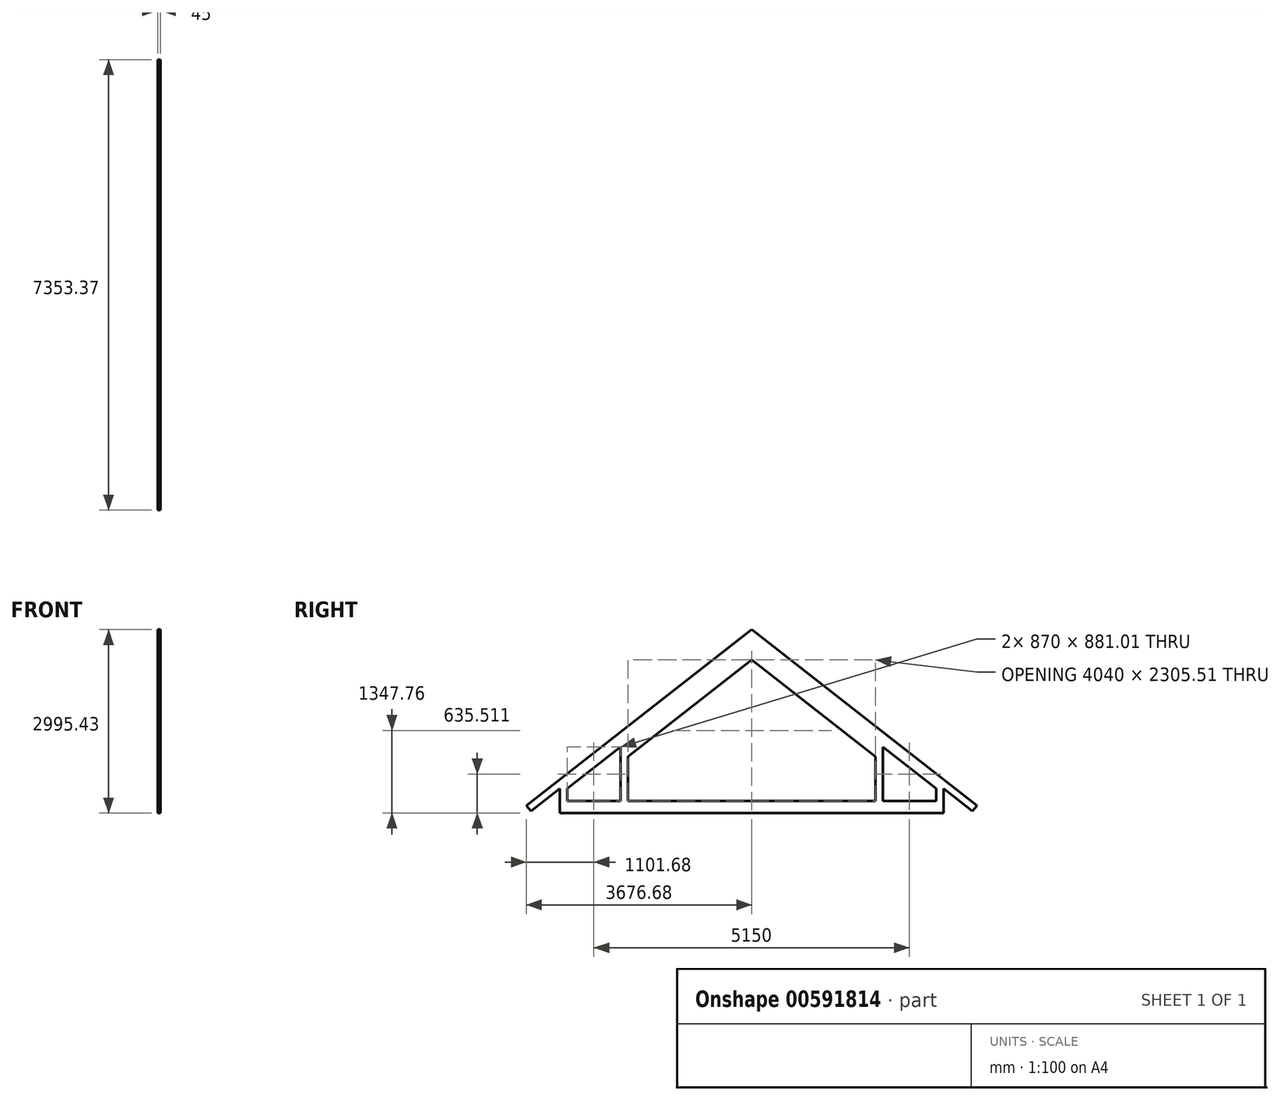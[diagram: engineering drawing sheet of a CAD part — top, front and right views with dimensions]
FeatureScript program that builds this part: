
annotation { "Feature Type Name" : "Feature", "Feature Type Description" : "" }
export const myFeature = defineFeature(function(context is Context, id is Id, definition is map)
    precondition{}
    {
        {
            var Q0;
            Q0=qCreatedBy(makeId("Right.planeOp"),FACE);
            var sketch = newSketch(context, id + "F0", { "sketchPlane" : qUnion([Q0]), "disableImprinting" : false});
            skLineSegment(sketch, "E0", {"start": v(-3120, 2101.32) * mm, "end": v(-3120, 2589.9) * mm});
            skLineSegment(sketch, "E1", {"start": v(-6240, 0) * mm, "end": v(-3120, 2437.61) * mm});
            skLineSegment(sketch, "E2", {"start": v(-3120, 2437.61) * mm, "end": v(0, 0) * mm});
            skLineSegment(sketch, "E3", {"start": v(-3120, 2589.9) * mm, "end": v(-6707.88, -213.27) * mm});
            skLineSegment(sketch, "E4", {"start": v(-3120, 2589.9) * mm, "end": v(467.88, -213.27) * mm});
            skLineSegment(sketch, "E5.0", {"start": v(-3120, 2101.32) * mm, "end": v(-1222.76, 619.04) * mm});
            skLineSegment(sketch, "E6", {"start": v(-1222.76, 619.04) * mm, "end": v(-1222.76, -172.9) * mm});
            skLineSegment(sketch, "E7", {"start": v(-5017.24, 619.04) * mm, "end": v(-5017.24, -172.9) * mm});
            skLineSegment(sketch, "E8.trimOffspring", {"start": v(-5017.24, 619.04) * mm, "end": v(-3120, 2101.32) * mm});
            skPoint(sketch, "E9.orphan", {"position": v(-3120, 0) * mm});
            skLineSegment(sketch, "E10.0", {"start": v(-3120, 2285.33) * mm, "end": v(-194.91, 0) * mm});
            skLineSegment(sketch, "E10.1", {"start": v(-6045.09, 0) * mm, "end": v(-3120, 2285.33) * mm});
            skLineSegment(sketch, "E11", {"start": v(-6240, 0) * mm, "end": v(-6045.09, 0) * mm});
            skLineSegment(sketch, "E12", {"start": v(0, 0) * mm, "end": v(-194.91, 0) * mm});
            skLineSegment(sketch, "E13", {"start": v(-1222.76, 619.04) * mm, "end": v(-1222.76, 803.04) * mm});
            skLineSegment(sketch, "E14", {"start": v(-5017.24, 619.04) * mm, "end": v(-5017.24, 803.04) * mm});
            skLineSegment(sketch, "E15.0", {"start": v(-5137.24, 600) * mm, "end": v(-5137.24, -172.9) * mm});
            skLineSegment(sketch, "E15.1", {"start": v(-5137.24, 600) * mm, "end": v(-5137.24, 709.29) * mm});
            skLineSegment(sketch, "E16.0", {"start": v(-1102.76, 600) * mm, "end": v(-1102.76, 709.29) * mm});
            skLineSegment(sketch, "E16.1", {"start": v(-1102.76, 600) * mm, "end": v(-1102.76, -172.9) * mm});
            skLineSegment(sketch, "E17", {"start": v(-1222.76, -400) * mm, "end": v(-1102.76, -400) * mm});
            skLineSegment(sketch, "E18", {"start": v(-5017.24, -342.9) * mm, "end": v(-5137.24, -342.9) * mm});
            skLineSegment(sketch, "E19", {"start": v(-6240, 0) * mm, "end": v(-6634, -307.83) * mm});
            skLineSegment(sketch, "E20", {"start": v(-6634, -307.83) * mm, "end": v(-6707.88, -213.27) * mm});
            skLineSegment(sketch, "E21", {"start": v(0, 0) * mm, "end": v(394, -307.83) * mm});
            skLineSegment(sketch, "E22", {"start": v(394, -307.83) * mm, "end": v(467.88, -213.27) * mm});
            skLineSegment(sketch, "E23", {"start": v(-6240, 0) * mm, "end": v(-6240, -342.9) * mm});
            skLineSegment(sketch, "E24", {"start": v(-6240, -342.9) * mm, "end": v(0, -342.9) * mm});
            skLineSegment(sketch, "E25", {"start": v(0, 0) * mm, "end": v(0, -342.9) * mm});
            skLineSegment(sketch, "E26.0", {"start": v(-6120, 0) * mm, "end": v(-6120, -172.9) * mm});
            skLineSegment(sketch, "E26.2", {"start": v(-120, 0) * mm, "end": v(-120, -172.9) * mm});
            skLineSegment(sketch, "E27.0", {"start": v(-6120, -172.9) * mm, "end": v(-5137.24, -172.9) * mm});
            skLineSegment(sketch, "E28.trimOffspring", {"start": v(-5017.24, -172.9) * mm, "end": v(-1222.76, -172.9) * mm});
            skLineSegment(sketch, "E29.trimOffspring", {"start": v(-1102.76, -172.9) * mm, "end": v(-120, -172.9) * mm});
            skLineSegment(sketch, "E30", {"start": v(6514.65, -342.9) * mm, "end": v(6514.65, 257.1) * mm});
            skLineSegment(sketch, "E31", {"start": v(6514.65, 257.1) * mm, "end": v(6038.7, -114.77) * mm});
            skLineSegment(sketch, "E32", {"start": v(6038.7, -114.77) * mm, "end": v(6094.1, -185.69) * mm});
            skLineSegment(sketch, "E33", {"start": v(6094.1, -185.69) * mm, "end": v(6514.65, 9.63) * mm});
            skLineSegment(sketch, "E34", {"start": v(6514.65, -342.9) * mm, "end": v(9634.65, -342.9) * mm});
            skLineSegment(sketch, "E35", {"start": v(9634.65, -342.9) * mm, "end": v(9634.65, 2695.1) * mm});
            skLineSegment(sketch, "E36", {"start": v(9634.65, 2695.1) * mm, "end": v(6514.65, 257.1) * mm});
            skLineSegment(sketch, "E37", {"start": v(6514.65, 9.63) * mm, "end": v(9634.65, 2447.24) * mm});
            skLineSegment(sketch, "E38", {"start": v(6514.65, -342.9) * mm, "end": v(6514.65, -147.9) * mm});
            skLineSegment(sketch, "E39", {"start": v(6514.65, -147.9) * mm, "end": v(9634.65, -147.9) * mm});
            skLineSegment(sketch, "E40", {"start": v(6514.65, -147.9) * mm, "end": v(6634.65, -147.9) * mm});
            skLineSegment(sketch, "E41", {"start": v(6634.65, -147.9) * mm, "end": v(6634.65, 103.39) * mm});
            skLineSegment(sketch, "E42", {"start": v(9634.65, -147.9) * mm, "end": v(7614.65, -147.9) * mm});
            skLineSegment(sketch, "E43", {"start": v(7614.65, -147.9) * mm, "end": v(7614.65, 869.05) * mm});
            skLineSegment(sketch, "E44", {"start": v(7614.65, 700.4) * mm, "end": v(9634.65, 2278.85) * mm});
            skLineSegment(sketch, "E45", {"start": v(7463.7, 751.1) * mm, "end": v(7463.7, -147.9) * mm});
            skLineSegment(sketch, "E46.MirrorCS", {"start": v(12754.65, -342.9) * mm, "end": v(12754.65, -147.9) * mm});
            skLineSegment(sketch, "E47.MirrorCS", {"start": v(13230.61, -114.77) * mm, "end": v(13175.2, -185.69) * mm});
            skLineSegment(sketch, "E48.MirrorCS", {"start": v(12754.65, -147.9) * mm, "end": v(12634.65, -147.9) * mm});
            skLineSegment(sketch, "E49.MirrorCS", {"start": v(12634.65, -147.9) * mm, "end": v(12634.65, 103.39) * mm});
            skLineSegment(sketch, "E50.MirrorCS", {"start": v(13175.2, -185.69) * mm, "end": v(12754.65, 9.63) * mm});
            skLineSegment(sketch, "E51.MirrorCS", {"start": v(12754.65, -342.9) * mm, "end": v(12754.65, 257.1) * mm});
            skLineSegment(sketch, "E52.MirrorCS", {"start": v(12754.65, 257.1) * mm, "end": v(13230.61, -114.77) * mm});
            skLineSegment(sketch, "E53.MirrorCS", {"start": v(12754.65, -342.9) * mm, "end": v(9634.65, -342.9) * mm});
            skLineSegment(sketch, "E54.MirrorCS", {"start": v(12754.65, -147.9) * mm, "end": v(9634.65, -147.9) * mm});
            skLineSegment(sketch, "E55.MirrorCS", {"start": v(9634.65, 2695.1) * mm, "end": v(12754.65, 257.1) * mm});
            skLineSegment(sketch, "E56.MirrorCS", {"start": v(11654.65, -147.9) * mm, "end": v(11654.65, 869.05) * mm});
            skLineSegment(sketch, "E57.MirrorCS", {"start": v(11805.62, 751.1) * mm, "end": v(11805.62, -147.9) * mm});
            skLineSegment(sketch, "E58.MirrorCS", {"start": v(9634.65, -147.9) * mm, "end": v(11654.65, -147.9) * mm});
            skLineSegment(sketch, "E59.MirrorCS", {"start": v(11654.65, 700.4) * mm, "end": v(9634.65, 2278.85) * mm});
            skLineSegment(sketch, "E60.MirrorCS", {"start": v(12754.65, 9.63) * mm, "end": v(9634.65, 2447.24) * mm});
            skLineSegment(sketch, "E61", {"start": v(0, -342.9) * mm, "end": v(0, 152.28) * mm});
            skLineSegment(sketch, "E62", {"start": v(3942.63, -4756.35) * mm, "end": v(7072.63, -4756.35) * mm});
            skLineSegment(sketch, "E63", {"start": v(7072.63, -4756.35) * mm, "end": v(7072.63, -4561.35) * mm});
            skLineSegment(sketch, "E64", {"start": v(3942.63, -4756.35) * mm, "end": v(3942.63, -4358.63) * mm});
            skLineSegment(sketch, "E65", {"start": v(3942.63, -4206.35) * mm, "end": v(3395.95, -4633.46) * mm});
            skLineSegment(sketch, "E66", {"start": v(3395.95, -4633.46) * mm, "end": v(3469.83, -4728.03) * mm});
            skLineSegment(sketch, "E67", {"start": v(3469.83, -4728.03) * mm, "end": v(3942.63, -4358.63) * mm});
            skLineSegment(sketch, "E68", {"start": v(3942.63, -4756.35) * mm, "end": v(3942.63, -4561.35) * mm});
            skLineSegment(sketch, "E69", {"start": v(3942.63, -4561.35) * mm, "end": v(7072.63, -4561.35) * mm});
            skLineSegment(sketch, "E70", {"start": v(3942.63, -4206.35) * mm, "end": v(7072.63, -1760.92) * mm});
            skLineSegment(sketch, "E71.0", {"start": v(4028.65, -4386.6) * mm, "end": v(7072.63, -2008.38) * mm});
            skLineSegment(sketch, "E72", {"start": v(4062.63, -4360.05) * mm, "end": v(4028.65, -4386.6) * mm});
            skLineSegment(sketch, "E73.0", {"start": v(4062.63, -4561.35) * mm, "end": v(4062.63, -4360.05) * mm});
            skLineSegment(sketch, "E74", {"start": v(3942.63, -4358.63) * mm, "end": v(4064.45, -4358.63) * mm});
            skLineSegment(sketch, "E75.trimOffspring", {"start": v(7072.63, -2008.38) * mm, "end": v(7072.63, -1760.92) * mm});
            skLineSegment(sketch, "E76", {"start": v(7072.63, -4756.35) * mm, "end": v(7072.63, -773.27) * mm});
            skLineSegment(sketch, "E77.0", {"start": v(5052.63, -3834.04) * mm, "end": v(7072.63, -2255.84) * mm});
            skLineSegment(sketch, "E78", {"start": v(7072.63, -4561.35) * mm, "end": v(5052.63, -4561.35) * mm});
            skLineSegment(sketch, "E79", {"start": v(5052.63, -4561.35) * mm, "end": v(5052.63, -3586.58) * mm});
            skLineSegment(sketch, "E80.0", {"start": v(4932.63, -4631.5) * mm, "end": v(4932.63, -3680.33) * mm});
            skLineSegment(sketch, "E81.MirrorCS", {"start": v(10082.63, -4360.05) * mm, "end": v(10116.62, -4386.6) * mm});
            skLineSegment(sketch, "E82.MirrorCS", {"start": v(10082.63, -4561.35) * mm, "end": v(10082.63, -4360.05) * mm});
            skLineSegment(sketch, "E83.MirrorCS", {"start": v(10202.63, -4358.63) * mm, "end": v(10080.81, -4358.63) * mm});
            skLineSegment(sketch, "E84.MirrorCS", {"start": v(10202.63, -4756.35) * mm, "end": v(10202.63, -4561.35) * mm});
            skLineSegment(sketch, "E85.MirrorCS", {"start": v(10202.63, -4756.35) * mm, "end": v(10202.63, -4358.63) * mm});
            skLineSegment(sketch, "E86.MirrorCS", {"start": v(10749.32, -4633.46) * mm, "end": v(10675.44, -4728.03) * mm});
            skLineSegment(sketch, "E87.MirrorCS", {"start": v(10675.44, -4728.03) * mm, "end": v(10202.63, -4358.63) * mm});
            skLineSegment(sketch, "E88.MirrorCS", {"start": v(9212.63, -4631.5) * mm, "end": v(9212.63, -3680.33) * mm});
            skLineSegment(sketch, "E89.MirrorCS", {"start": v(10202.63, -4561.35) * mm, "end": v(7072.63, -4561.35) * mm});
            skLineSegment(sketch, "E90.MirrorCS", {"start": v(10202.63, -4206.35) * mm, "end": v(10749.32, -4633.46) * mm});
            skLineSegment(sketch, "E91.MirrorCS", {"start": v(9092.63, -4561.35) * mm, "end": v(9092.63, -3586.58) * mm});
            skLineSegment(sketch, "E92.MirrorCS", {"start": v(7072.63, -4561.35) * mm, "end": v(9092.63, -4561.35) * mm});
            skLineSegment(sketch, "E93.MirrorCS", {"start": v(10116.62, -4386.6) * mm, "end": v(7072.63, -2008.38) * mm});
            skLineSegment(sketch, "E94.MirrorCS", {"start": v(10202.63, -4756.35) * mm, "end": v(7072.63, -4756.35) * mm});
            skLineSegment(sketch, "E95.MirrorCS", {"start": v(9092.63, -3834.04) * mm, "end": v(7072.63, -2255.84) * mm});
            skLineSegment(sketch, "E96.MirrorCS", {"start": v(10202.63, -4206.35) * mm, "end": v(7072.63, -1760.92) * mm});
            skLineSegment(sketch, "E97", {"start": v(7072.63, -4561.35) * mm, "end": v(7072.63, -2511.35) * mm});
            skPoint(sketch, "E98.orphan", {"position": v(7072.63, -2255.84) * mm});
            skLineSegment(sketch, "E99.bottom", {"start": v(-19664, -11770.7) * mm, "end": v(-17264, -11770.7) * mm});
            skLineSegment(sketch, "E99.top", {"start": v(-19664, -14570.7) * mm, "end": v(-17264, -14570.7) * mm});
            skLineSegment(sketch, "E99.left", {"start": v(-19664, -11770.7) * mm, "end": v(-19664, -14570.7) * mm});
            skLineSegment(sketch, "E99.right", {"start": v(-17264, -11770.7) * mm, "end": v(-17264, -14570.7) * mm});
            skLineSegment(sketch, "E100", {"start": v(-17264, -14570.7) * mm, "end": v(-17263.63, -11819.7) * mm});
            skSolve(sketch);
        }
        {
            var Q0;
            {var subQ4=sQuery(id+"F0.wireOp",EDGE,"E83.MirrorCS");Q0=makeQuery(id+"F0.imprint","IMPRINT",FACE,{"disambiguationData":[TD([[makeQuery(id+"F0.imprint","IMPRINT",EDGE,{"derivedFrom":subQ4}),-1.0]])]});}
            var Q1;
            {var subQ3=sQuery(id+"F0.wireOp",EDGE,"E95.MirrorCS");Q1=makeQuery(id+"F0.imprint","IMPRINT",FACE,{"disambiguationData":[TD([[makeQuery(id+"F0.imprint","IMPRINT",EDGE,{"derivedFrom":subQ3}),-1.0]])]});}
            var Q2;
            Q2=makeQuery(id+"F0.imprint","IMPRINT",FACE,{"disambiguationData":[TD([[makeQuery(id+"F0.imprint","IMPRINT",EDGE,{"derivedFrom":sQuery(id+"F0.wireOp",EDGE,"E65")}),1.0]])]});
            var Q3;
            {var subQ5=sQuery(id+"F0.wireOp",EDGE,"E77.0");Q3=makeQuery(id+"F0.imprint","IMPRINT",FACE,{"disambiguationData":[TD([[makeQuery(id+"F0.imprint","IMPRINT",EDGE,{"derivedFrom":subQ5}),1.0]])]});}
            var Q4;
            {var subQ6=sQuery(id+"F0.wireOp",EDGE,"E80.0");Q4=makeQuery(id+"F0.imprint","IMPRINT",FACE,{"disambiguationData":[TD([[makeQuery(id+"F0.imprint","IMPRINT",EDGE,{"derivedFrom":subQ6}),-1.0]])]});}
            var Q5;
            {var subQ4=sQuery(id+"F0.wireOp",EDGE,"E64");Q5=makeQuery(id+"F0.imprint","IMPRINT",FACE,{"disambiguationData":[TD([[makeQuery(id+"F0.imprint","IMPRINT",EDGE,{"derivedFrom":subQ4}),-1.0]])]});}
            var Q6;
            Q6=makeQuery(id+"F0.imprint","IMPRINT",FACE,{"disambiguationData":[TD([[makeQuery(id+"F0.imprint","IMPRINT",EDGE,{"derivedFrom":sQuery(id+"F0.wireOp",EDGE,"E62")}),1.0]])]});
            var Q7;
            Q7=makeQuery(id+"F0.imprint","IMPRINT",FACE,{"disambiguationData":[TD([[makeQuery(id+"F0.imprint","IMPRINT",EDGE,{"derivedFrom":sQuery(id+"F0.wireOp",EDGE,"E63")}),-1.0]])]});
            var Q8;
            {var subQ5=sQuery(id+"F0.wireOp",EDGE,"E88.MirrorCS");Q8=makeQuery(id+"F0.imprint","IMPRINT",FACE,{"disambiguationData":[TD([[makeQuery(id+"F0.imprint","IMPRINT",EDGE,{"derivedFrom":subQ5}),1.0]])]});}
            var Q9;
            {var subQ5=sQuery(id+"F0.wireOp",EDGE,"E81.MirrorCS");Q9=makeQuery(id+"F0.imprint","IMPRINT",FACE,{"disambiguationData":[TD([[makeQuery(id+"F0.imprint","IMPRINT",EDGE,{"derivedFrom":subQ5}),1.0]])]});}
            var Q10;
            {var subQ1=sQuery(id+"F0.wireOp",EDGE,"E82.MirrorCS");Q10=makeQuery(id+"F0.imprint","IMPRINT",FACE,{"disambiguationData":[TD([[makeQuery(id+"F0.imprint","IMPRINT",EDGE,{"derivedFrom":subQ1}),-1.0]])]});}
            extrude(context, id + "F1", {"entities" : qUnion([Q0, Q1, Q2, Q3, Q4, Q5, Q6, Q7, Q8, Q9, Q10]), "depth" : 45 * mm, "offsetDistance" : 25 * mm});
        }
    });
